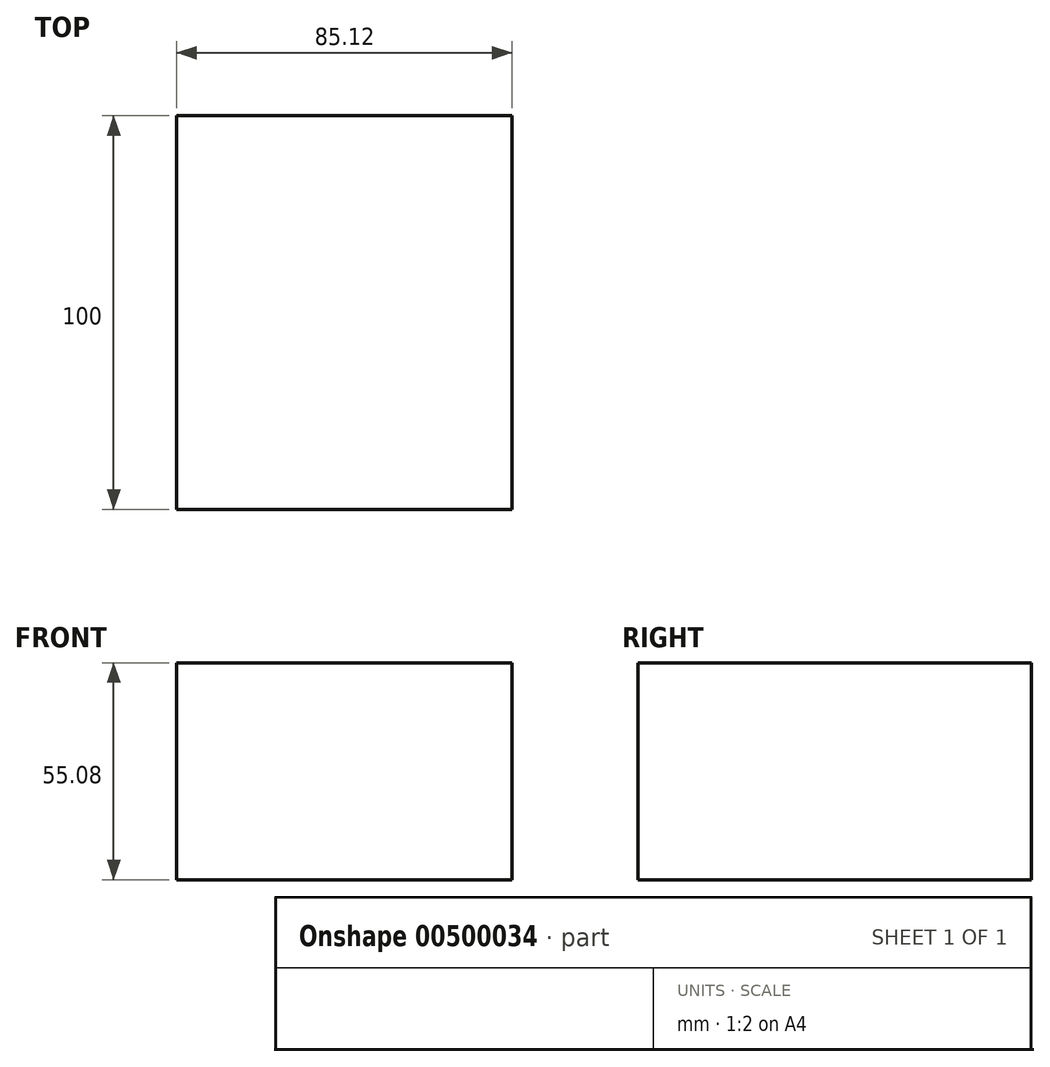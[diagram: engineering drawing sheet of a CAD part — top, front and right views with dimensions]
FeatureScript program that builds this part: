
annotation { "Feature Type Name" : "Feature", "Feature Type Description" : "" }
export const myFeature = defineFeature(function(context is Context, id is Id, definition is map)
    precondition{}
    {
        {
            var Q0;
            Q0=qCreatedBy(makeId("Front.planeOp"),FACE);
            var sketch = newSketch(context, id + "F0", { "sketchPlane" : qUnion([Q0])});
            skLineSegment(sketch, "E0.bottom", {"start": v(42.56, 27.54) * mm, "end": v(-42.56, 27.54) * mm});
            skLineSegment(sketch, "E0.top", {"start": v(42.56, -27.54) * mm, "end": v(-42.56, -27.54) * mm});
            skLineSegment(sketch, "E0.left", {"start": v(42.56, 27.54) * mm, "end": v(42.56, -27.54) * mm});
            skLineSegment(sketch, "E0.right", {"start": v(-42.56, 27.54) * mm, "end": v(-42.56, -27.54) * mm});
            skPoint(sketch, "E0.middle", {"position": v(0, 0) * mm});
            skSolve(sketch);
        }
        {
            var Q0;
            Q0 = qSketchRegion(id + "F0", true);
            extrude(context, id + "F1", {"entities" : qUnion([Q0]), "endBound" : BoundingType.SYMMETRIC, "depth" : 100 * mm});
        }
    });
